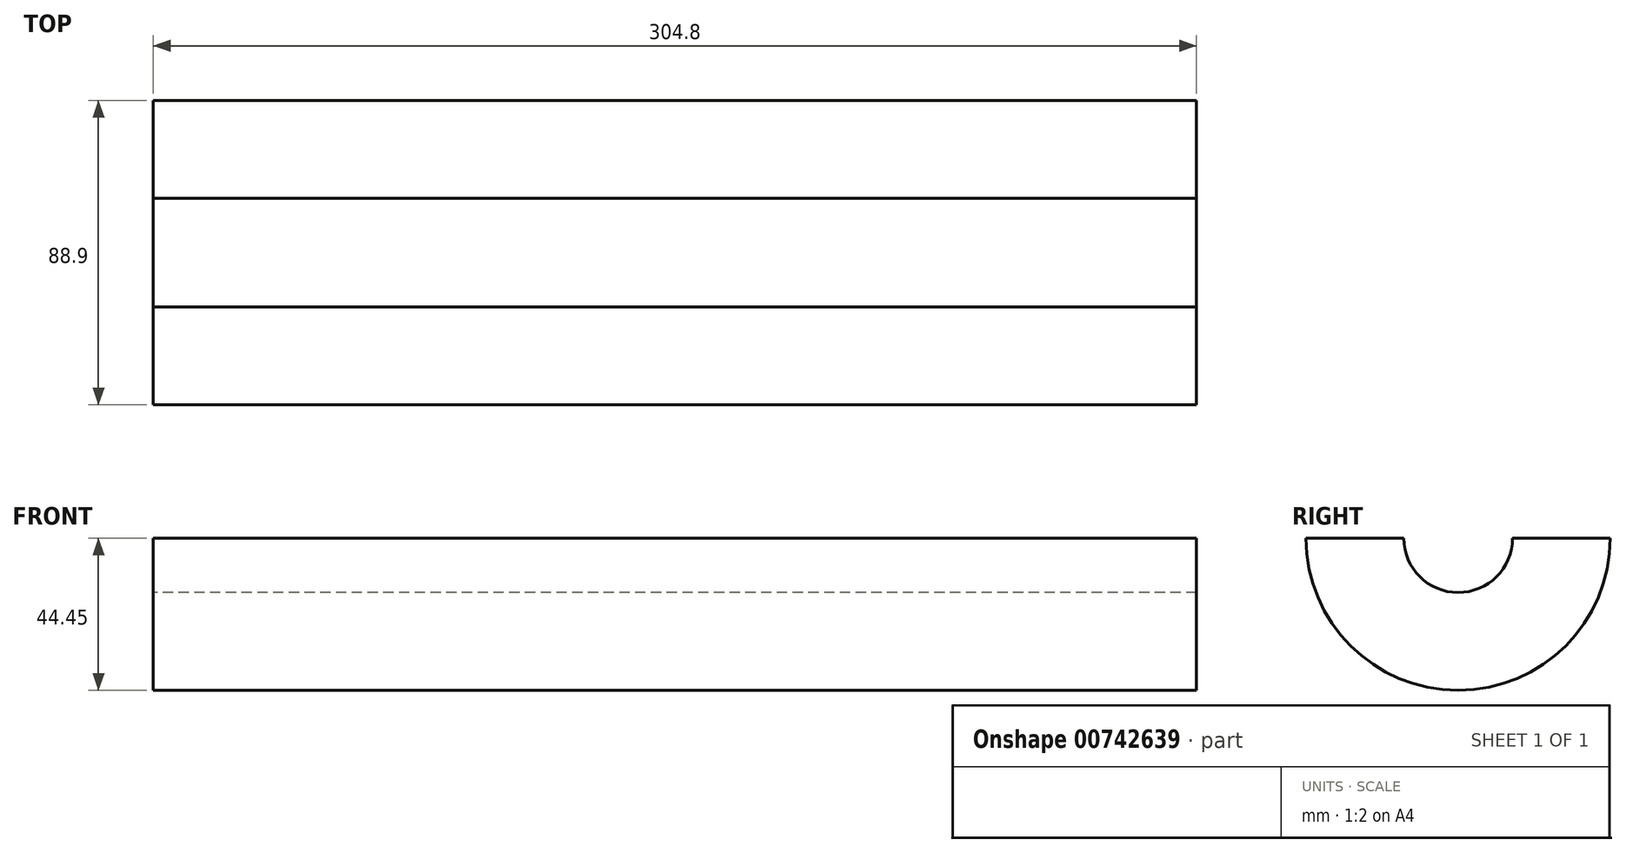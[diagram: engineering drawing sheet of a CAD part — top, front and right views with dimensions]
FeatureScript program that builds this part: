
annotation { "Feature Type Name" : "Feature", "Feature Type Description" : "" }
export const myFeature = defineFeature(function(context is Context, id is Id, definition is map)
    precondition{}
    {
        {
            var Q0;
            Q0=qCreatedBy(makeId("Right.planeOp"),FACE);
            var sketch = newSketch(context, id + "F0", { "sketchPlane" : qUnion([Q0])});
            skArc(sketch, "E0", {"start": v(-44.45, 0) * mm, "mid": v(0, -44.45) * mm, "end": v(44.45, 0) * mm});
            skArc(sketch, "E1", {"start": v(-15.88, 0) * mm, "mid": v(0, -15.88) * mm, "end": v(15.88, 0) * mm});
            skLineSegment(sketch, "E2", {"start": v(15.88, 0) * mm, "end": v(44.45, 0) * mm});
            skLineSegment(sketch, "E3", {"start": v(-15.88, 0) * mm, "end": v(-44.45, 0) * mm});
            skSolve(sketch);
        }
        {
            var Q0;
            Q0=makeQuery(id+"F0.imprint","IMPRINT",FACE,{"disambiguationData":[TD([[makeQuery(id+"F0.imprint","IMPRINT",EDGE,{"derivedFrom":sQuery(id+"F0.wireOp",EDGE,"E0")}),1.0]])]});
            extrude(context, id + "F1", {"entities" : qUnion([Q0]), "depth" : 304.8 * mm, "offsetDistance" : 25.4 * mm});
        }
    });
